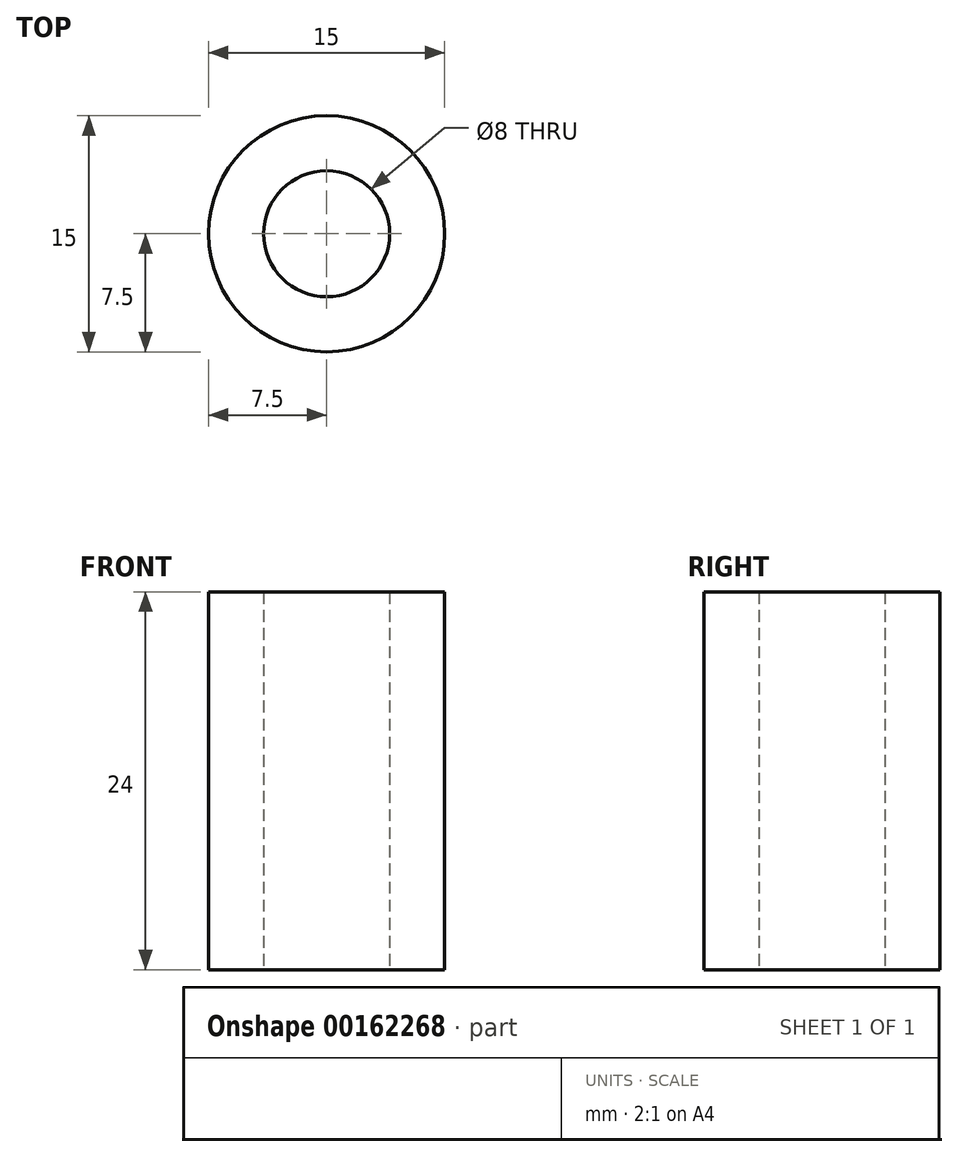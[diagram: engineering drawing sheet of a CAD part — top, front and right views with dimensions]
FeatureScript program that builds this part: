
annotation { "Feature Type Name" : "Feature", "Feature Type Description" : "" }
export const myFeature = defineFeature(function(context is Context, id is Id, definition is map)
    precondition{}
    {
        {
            var Q0;
            Q0=qCreatedBy(makeId("Top.planeOp"),FACE);
            var sketch = newSketch(context, id + "F0", { "sketchPlane" : qUnion([Q0])});
            skCircle(sketch, "E0", {"center": v(0, 0) * mm, "radius": 7.5 * mm});
            skCircle(sketch, "E1", {"center": v(0, 0) * mm, "radius": 4 * mm});
            skSolve(sketch);
        }
        {
            var Q0;
            Q0 = qSketchRegion(id + "F0", true);
            extrude(context, id + "F1", {"entities" : qUnion([Q0]), "depth" : 24 * mm});
        }
    });
